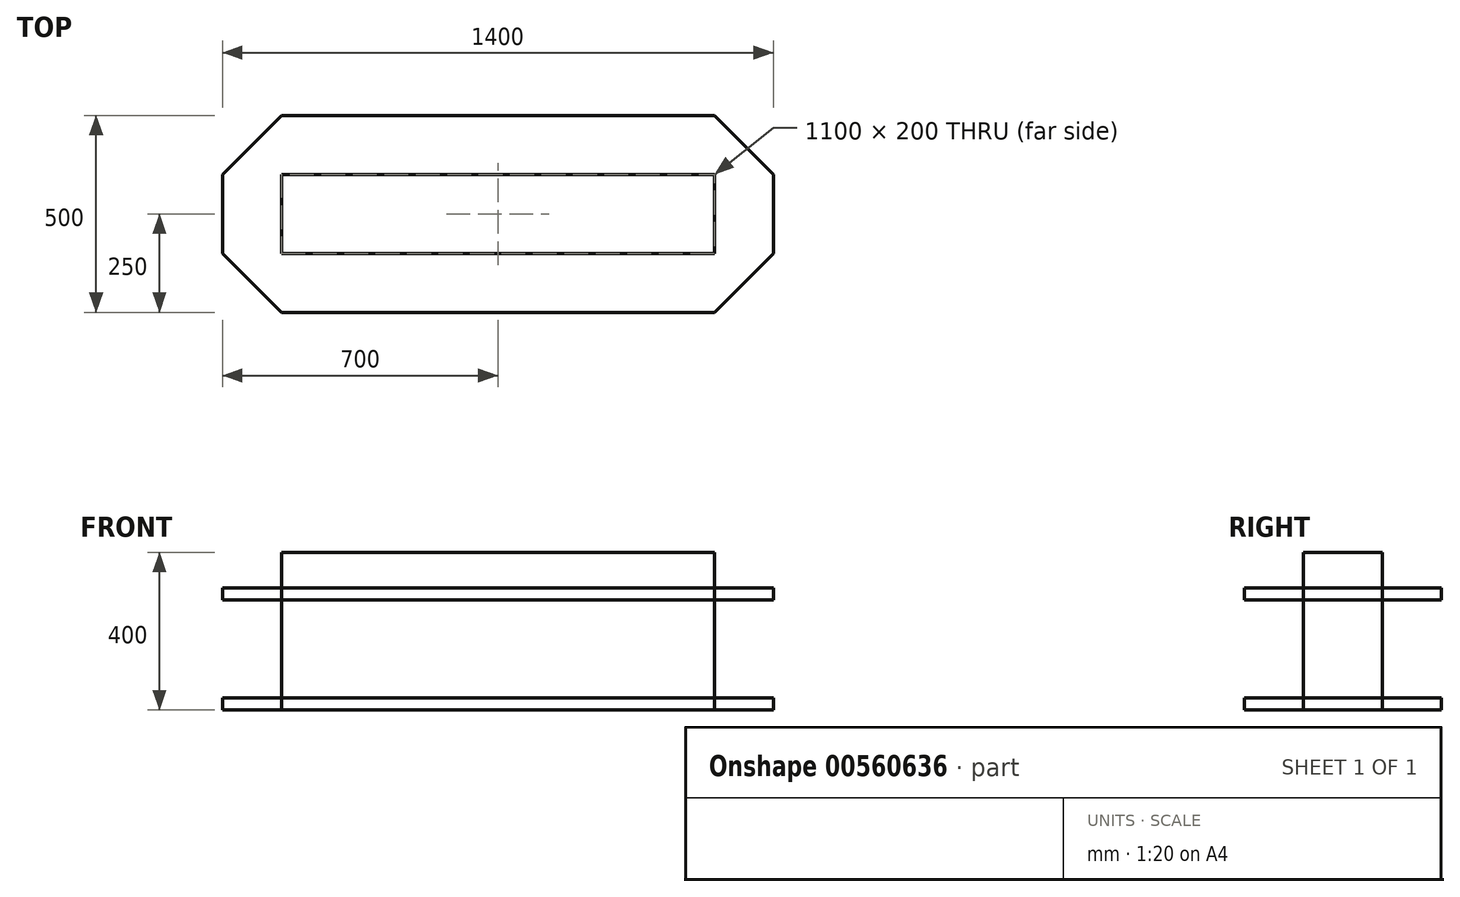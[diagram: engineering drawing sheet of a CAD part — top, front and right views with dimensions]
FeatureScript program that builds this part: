
annotation { "Feature Type Name" : "Feature", "Feature Type Description" : "" }
export const myFeature = defineFeature(function(context is Context, id is Id, definition is map)
    precondition{}
    {
        {
            var Q0;
            Q0=qCreatedBy(makeId("Top.planeOp"),FACE);
            var sketch = newSketch(context, id + "F0", { "sketchPlane" : qUnion([Q0])});
            skLineSegment(sketch, "E0.bottom", {"start": v(0, 0) * mm, "end": v(1400, 0) * mm});
            skLineSegment(sketch, "E0.top", {"start": v(0, -500) * mm, "end": v(1400, -500) * mm});
            skLineSegment(sketch, "E0.left", {"start": v(0, 0) * mm, "end": v(0, -500) * mm});
            skLineSegment(sketch, "E0.right", {"start": v(1400, 0) * mm, "end": v(1400, -500) * mm});
            skLineSegment(sketch, "E1", {"start": v(0, -150) * mm, "end": v(150, 0) * mm});
            skLineSegment(sketch, "E2", {"start": v(0, -350) * mm, "end": v(150, -500) * mm});
            skLineSegment(sketch, "E3", {"start": v(1250, -500) * mm, "end": v(1400, -350) * mm});
            skLineSegment(sketch, "E4", {"start": v(1400, -150) * mm, "end": v(1250, 0) * mm});
            skSolve(sketch);
        }
        {
            var Q0;
            {var subQ3=sQuery(id+"F0.wireOp",EDGE,"E1");Q0=makeQuery(id+"F0.imprint","IMPRINT",FACE,{"disambiguationData":[TD([[makeQuery(id+"F0.imprint","IMPRINT",EDGE,{"derivedFrom":subQ3}),-1.0]])]});}
            extrude(context, id + "F1", {"entities" : qUnion([Q0]), "depth" : 400 * mm, "offsetDistance" : 25 * mm});
        }
        {
            var Q0;
            Q0=makeQuery(id+"F1.opExtrude","SWEPT_FACE",FACE,{"disambiguationData":[OSD([sQuery(id+"F0.wireOp",EDGE,"E0.bottom")])]});
            var sketch = newSketch(context, id + "F2", { "sketchPlane" : qUnion([Q0])});
            skLineSegment(sketch, "E5.bottom", {"start": v(0, 30) * mm, "end": v(-1400, 30) * mm});
            skLineSegment(sketch, "E5.top", {"start": v(0, 280) * mm, "end": v(-1400, 280) * mm});
            skLineSegment(sketch, "E5.left", {"start": v(0, 30) * mm, "end": v(0, 280) * mm});
            skLineSegment(sketch, "E5.right", {"start": v(-1400, 30) * mm, "end": v(-1400, 280) * mm});
            skLineSegment(sketch, "E6.bottom", {"start": v(0, 310) * mm, "end": v(-1400, 310) * mm});
            skLineSegment(sketch, "E6.top", {"start": v(0, 400) * mm, "end": v(-1400, 400) * mm});
            skLineSegment(sketch, "E6.left", {"start": v(0, 310) * mm, "end": v(0, 400) * mm});
            skLineSegment(sketch, "E6.right", {"start": v(-1400, 310) * mm, "end": v(-1400, 400) * mm});
            skSolve(sketch);
        }
        {
            var Q0;
            Q0 = qSketchRegion(id + "F2", true);
            extrude(context, id + "F3", {"entities" : qUnion([Q0]), "operationType" : NewBodyOperationType.REMOVE, "endBound" : BoundingType.THROUGH_ALL, "oppositeDirection" : true, "depth" : 25 * mm, "offsetDistance" : 25 * mm});
        }
        {
            var Q0;
            Q0=makeQuery(id+"F1.opExtrude","CAP_FACE",FACE,{"disambiguationData":[OSD([sQuery(id+"F0.wireOp",EDGE,"E0.bottom"),sQuery(id+"F0.wireOp",EDGE,"E0.top"),sQuery(id+"F0.wireOp",EDGE,"E0.left"),sQuery(id+"F0.wireOp",EDGE,"E0.right"),sQuery(id+"F0.wireOp",EDGE,"E1"),sQuery(id+"F0.wireOp",EDGE,"E2"),sQuery(id+"F0.wireOp",EDGE,"E3"),sQuery(id+"F0.wireOp",EDGE,"E4")])],"isStart":true});
            var sketch = newSketch(context, id + "F4", { "sketchPlane" : qUnion([Q0])});
            skLineSegment(sketch, "E7.bottom", {"start": v(150, 350) * mm, "end": v(1250, 350) * mm});
            skLineSegment(sketch, "E7.top", {"start": v(150, 150) * mm, "end": v(1250, 150) * mm});
            skLineSegment(sketch, "E7.left", {"start": v(150, 350) * mm, "end": v(150, 150) * mm});
            skLineSegment(sketch, "E7.right", {"start": v(1250, 350) * mm, "end": v(1250, 150) * mm});
            skSolve(sketch);
        }
        {
            var Q0;
            Q0 = qSketchRegion(id + "F4", true);
            extrude(context, id + "F5", {"entities" : qUnion([Q0]), "operationType" : NewBodyOperationType.ADD, "oppositeDirection" : true, "depth" : 400 * mm, "offsetDistance" : 25 * mm});
        }
    });
